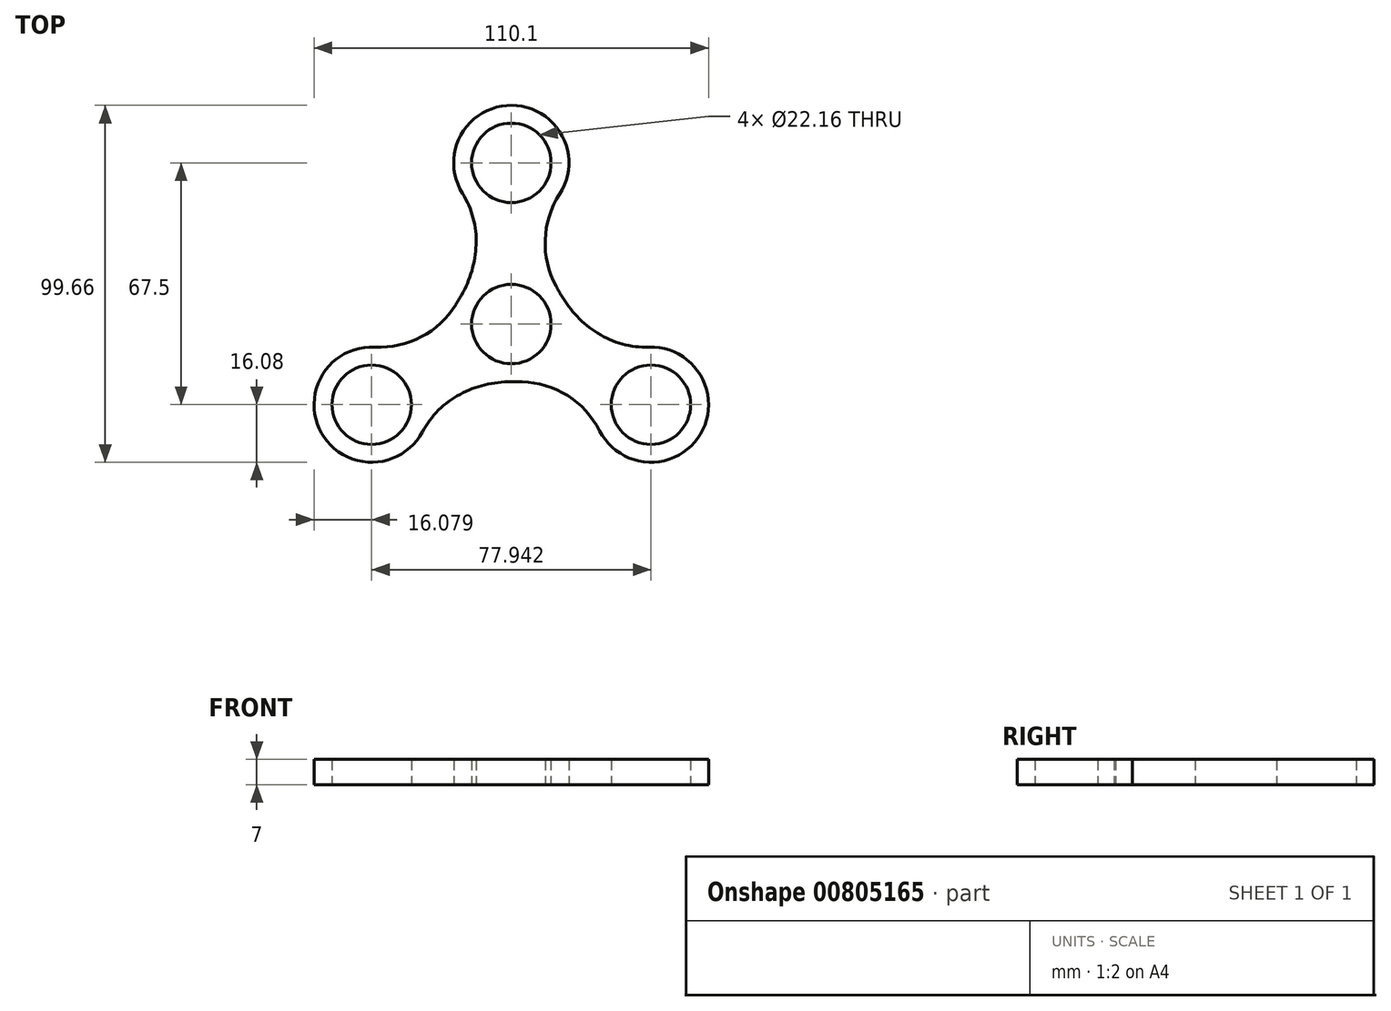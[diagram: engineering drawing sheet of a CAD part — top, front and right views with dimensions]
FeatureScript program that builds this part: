
annotation { "Feature Type Name" : "Feature", "Feature Type Description" : "" }
export const myFeature = defineFeature(function(context is Context, id is Id, definition is map)
    precondition{}
    {
        {
            var Q0;
            Q0=qCreatedBy(makeId("Top.planeOp"),FACE);
            var sketch = newSketch(context, id + "F0", { "sketchPlane" : qUnion([Q0])});
            skCircle(sketch, "E0", {"center": v(0, 0) * mm, "radius": 16.08 * mm});
            skLineSegment(sketch, "E1", {"start": v(0, 0) * mm, "end": v(0, 45) * mm, "construction": true});
            skLineSegment(sketch, "E2.1.0", {"start": v(0, 0) * mm, "end": v(-38.97, -22.5) * mm, "construction": true});
            skLineSegment(sketch, "E2.2.0", {"start": v(0, 0) * mm, "end": v(38.97, -22.5) * mm, "construction": true});
            skArc(sketch, "E3", {"start": v(-38.97, -22.5) * mm, "mid": v(-13.93, 8.04) * mm, "end": v(0, 45) * mm});
            skCircle(sketch, "E4", {"center": v(0, 0) * mm, "radius": 11.08 * mm});
            skArc(sketch, "E5", {"start": v(0, 45) * mm, "mid": v(13.93, 8.04) * mm, "end": v(38.97, -22.5) * mm});
            skArc(sketch, "E6", {"start": v(38.97, -22.5) * mm, "mid": v(0, -16.08) * mm, "end": v(-38.97, -22.5) * mm});
            skCircle(sketch, "E7", {"center": v(0, 45) * mm, "radius": 11.08 * mm});
            skCircle(sketch, "E8", {"center": v(0, 45) * mm, "radius": 16.08 * mm});
            skCircle(sketch, "E9.1.0", {"center": v(-38.97, -22.5) * mm, "radius": 16.08 * mm});
            skCircle(sketch, "E9.1.1", {"center": v(-38.97, -22.5) * mm, "radius": 11.08 * mm});
            skCircle(sketch, "E9.2.0", {"center": v(38.97, -22.5) * mm, "radius": 16.08 * mm});
            skCircle(sketch, "E9.2.1", {"center": v(38.97, -22.5) * mm, "radius": 11.08 * mm});
            skLineSegment(sketch, "E10", {"start": v(-30.41, 33.92) * mm, "end": v(35.6, 33.92) * mm, "construction": true});
            skArc(sketch, "E11", {"start": v(-13.93, 8.04) * mm, "mid": v(-9.92, 20.73) * mm, "end": v(-11.65, 33.92) * mm});
            skLineSegment(sketch, "E12", {"start": v(-119.14, 68.79) * mm, "end": v(0, -137.57) * mm, "construction": true});
            skLineSegment(sketch, "E13", {"start": v(0, -137.57) * mm, "end": v(119.14, 68.79) * mm, "construction": true});
            skLineSegment(sketch, "E14", {"start": v(119.14, 68.79) * mm, "end": v(-119.14, 68.79) * mm, "construction": true});
            skArc(sketch, "E15.MirrorCS", {"start": v(13.93, 8.04) * mm, "mid": v(9.92, 20.73) * mm, "end": v(11.65, 33.92) * mm});
            skArc(sketch, "E16.1.0", {"start": v(0, -16.08) * mm, "mid": v(-12.99, -18.96) * mm, "end": v(-23.55, -27.05) * mm});
            skArc(sketch, "E16.1.1", {"start": v(-13.93, 8.04) * mm, "mid": v(-22.91, -1.77) * mm, "end": v(-35.2, -6.87) * mm});
            skArc(sketch, "E16.2.0", {"start": v(13.93, 8.04) * mm, "mid": v(22.91, -1.77) * mm, "end": v(35.2, -6.87) * mm});
            skArc(sketch, "E16.2.1", {"start": v(0, -16.08) * mm, "mid": v(12.99, -18.96) * mm, "end": v(23.55, -27.05) * mm});
            skSolve(sketch);
        }
        {
            var Q0;
            {var subQ0=sQuery(id+"F0.wireOp",EDGE,"E8");var subQ2=sQuery(id+"F0.wireOp",EDGE,"E3");var subQ3=makeQuery(id+"F0.imprint","INTERSECT",VERTEX,{"derivedFrom":[subQ2,subQ0]});Q0=makeQuery(id+"F0.imprint","IMPRINT",FACE,{"disambiguationData":[TD([[makeQuery(id+"F0.imprint","IMPRINT",EDGE,{"disambiguationData":[TD([[subQ3,-1.0]])],"derivedFrom":subQ2}),1.0]])]});}
            var Q1;
            {var subQ0=sQuery(id+"F0.wireOp",EDGE,"E11");Q1=makeQuery(id+"F0.imprint","IMPRINT",FACE,{"disambiguationData":[TD([[makeQuery(id+"F0.imprint","IMPRINT",EDGE,{"derivedFrom":subQ0}),-1.0]])]});}
            var Q2;
            {var subQ0=sQuery(id+"F0.wireOp",EDGE,"E8");var subQ1=sQuery(id+"F0.wireOp",EDGE,"E3");var subQ2=makeQuery(id+"F0.imprint","INTERSECT",VERTEX,{"derivedFrom":[subQ1,subQ0]});Q2=makeQuery(id+"F0.imprint","IMPRINT",FACE,{"disambiguationData":[TD([[makeQuery(id+"F0.imprint","IMPRINT",EDGE,{"disambiguationData":[TD([[subQ2,-1.0]])],"derivedFrom":subQ1}),-1.0]])]});}
            var Q3;
            {var subQ0=sQuery(id+"F0.wireOp",EDGE,"E3");var subQ5=sQuery(id+"F0.wireOp",EDGE,"E8");var subQ6=makeQuery(id+"F0.imprint","INTERSECT",VERTEX,{"derivedFrom":[subQ0,subQ5]});Q3=makeQuery(id+"F0.imprint","IMPRINT",FACE,{"disambiguationData":[TD([[makeQuery(id+"F0.imprint","IMPRINT",EDGE,{"disambiguationData":[TD([[subQ6,-1.0]])],"derivedFrom":subQ5}),-1.0]])]});}
            var Q4;
            {var subQ0=sQuery(id+"F0.wireOp",EDGE,"E15.MirrorCS");Q4=makeQuery(id+"F0.imprint","IMPRINT",FACE,{"disambiguationData":[TD([[makeQuery(id+"F0.imprint","IMPRINT",EDGE,{"derivedFrom":subQ0}),1.0]])]});}
            var Q5;
            {var subQ5=sQuery(id+"F0.wireOp",EDGE,"E3");var subQ7=sQuery(id+"F0.wireOp",EDGE,"E9.1.1");var subQ9=makeQuery(id+"F0.imprint","INTERSECT",VERTEX,{"derivedFrom":[subQ5,subQ7]});Q5=makeQuery(id+"F0.imprint","IMPRINT",FACE,{"disambiguationData":[TD([[makeQuery(id+"F0.imprint","IMPRINT",EDGE,{"disambiguationData":[TD([[subQ9,-1.0]])],"derivedFrom":subQ5}),1.0]])]});}
            var Q6;
            {var subQ0=sQuery(id+"F0.wireOp",EDGE,"E9.1.1");var subQ1=sQuery(id+"F0.wireOp",EDGE,"E3");var subQ2=makeQuery(id+"F0.imprint","INTERSECT",VERTEX,{"derivedFrom":[subQ1,subQ0]});Q6=makeQuery(id+"F0.imprint","IMPRINT",FACE,{"disambiguationData":[TD([[makeQuery(id+"F0.imprint","IMPRINT",EDGE,{"disambiguationData":[TD([[subQ2,-1.0]])],"derivedFrom":subQ1}),-1.0]])]});}
            var Q7;
            {var subQ0=sQuery(id+"F0.wireOp",EDGE,"E16.1.1");Q7=makeQuery(id+"F0.imprint","IMPRINT",FACE,{"disambiguationData":[TD([[makeQuery(id+"F0.imprint","IMPRINT",EDGE,{"derivedFrom":subQ0}),1.0]])]});}
            var Q8;
            {var subQ0=sQuery(id+"F0.wireOp",EDGE,"E3");var subQ5=sQuery(id+"F0.wireOp",EDGE,"E9.1.0");var subQ6=makeQuery(id+"F0.imprint","INTERSECT",VERTEX,{"derivedFrom":[subQ0,subQ5]});Q8=makeQuery(id+"F0.imprint","IMPRINT",FACE,{"disambiguationData":[TD([[makeQuery(id+"F0.imprint","IMPRINT",EDGE,{"disambiguationData":[TD([[subQ6,1.0]])],"derivedFrom":subQ5}),-1.0]])]});}
            var Q9;
            {var subQ0=sQuery(id+"F0.wireOp",EDGE,"E16.1.0");Q9=makeQuery(id+"F0.imprint","IMPRINT",FACE,{"disambiguationData":[TD([[makeQuery(id+"F0.imprint","IMPRINT",EDGE,{"derivedFrom":subQ0}),-1.0]])]});}
            var Q10;
            {var subQ0=sQuery(id+"F0.wireOp",EDGE,"E5");var subQ5=sQuery(id+"F0.wireOp",EDGE,"E9.2.0");var subQ6=makeQuery(id+"F0.imprint","INTERSECT",VERTEX,{"derivedFrom":[subQ0,subQ5]});Q10=makeQuery(id+"F0.imprint","IMPRINT",FACE,{"disambiguationData":[TD([[makeQuery(id+"F0.imprint","IMPRINT",EDGE,{"disambiguationData":[TD([[subQ6,-1.0]])],"derivedFrom":subQ5}),-1.0]])]});}
            var Q11;
            {var subQ0=sQuery(id+"F0.wireOp",EDGE,"E16.2.1");Q11=makeQuery(id+"F0.imprint","IMPRINT",FACE,{"disambiguationData":[TD([[makeQuery(id+"F0.imprint","IMPRINT",EDGE,{"derivedFrom":subQ0}),1.0]])]});}
            var Q12;
            {var subQ0=sQuery(id+"F0.wireOp",EDGE,"E16.2.0");Q12=makeQuery(id+"F0.imprint","IMPRINT",FACE,{"disambiguationData":[TD([[makeQuery(id+"F0.imprint","IMPRINT",EDGE,{"derivedFrom":subQ0}),-1.0]])]});}
            var Q13;
            {var subQ0=sQuery(id+"F0.wireOp",EDGE,"E9.2.0");var subQ4=sQuery(id+"F0.wireOp",EDGE,"E5");var subQ5=makeQuery(id+"F0.imprint","INTERSECT",VERTEX,{"derivedFrom":[subQ4,subQ0]});Q13=makeQuery(id+"F0.imprint","IMPRINT",FACE,{"disambiguationData":[TD([[makeQuery(id+"F0.imprint","IMPRINT",EDGE,{"disambiguationData":[TD([[subQ5,-1.0]])],"derivedFrom":subQ4}),1.0]])]});}
            var Q14;
            {var subQ0=sQuery(id+"F0.wireOp",EDGE,"E9.2.0");var subQ1=sQuery(id+"F0.wireOp",EDGE,"E5");var subQ2=makeQuery(id+"F0.imprint","INTERSECT",VERTEX,{"derivedFrom":[subQ1,subQ0]});Q14=makeQuery(id+"F0.imprint","IMPRINT",FACE,{"disambiguationData":[TD([[makeQuery(id+"F0.imprint","IMPRINT",EDGE,{"disambiguationData":[TD([[subQ2,-1.0]])],"derivedFrom":subQ1}),-1.0]])]});}
            var Q15;
            Q15=makeQuery(id+"F0.imprint","IMPRINT",FACE,{"disambiguationData":[TD([[makeQuery(id+"F0.imprint","IMPRINT",EDGE,{"derivedFrom":sQuery(id+"F0.wireOp",EDGE,"E4")}),-1.0]])]});
            extrude(context, id + "F1", {"entities" : qUnion([Q0, Q1, Q2, Q3, Q4, Q5, Q6, Q7, Q8, Q9, Q10, Q11, Q12, Q13, Q14, Q15]), "depth" : 7 * mm, "offsetDistance" : 25 * mm});
        }
        {
            var Q0;
            Q0=makeQuery(id+"F1.opExtrude","SWEPT_EDGE",EDGE,{"disambiguationData":[OSD([sQuery(id+"F0.wireOp",EDGE,"E8"),sQuery(id+"F0.wireOp",EDGE,"E15.MirrorCS")])]});
            var Q1;
            Q1=makeQuery(id+"F1.opExtrude","SWEPT_EDGE",EDGE,{"disambiguationData":[OSD([sQuery(id+"F0.wireOp",EDGE,"E8"),sQuery(id+"F0.wireOp",EDGE,"E11")])]});
            var Q2;
            Q2=makeQuery(id+"F1.opExtrude","SWEPT_EDGE",EDGE,{"disambiguationData":[OSD([sQuery(id+"F0.wireOp",EDGE,"E9.2.0"),sQuery(id+"F0.wireOp",EDGE,"E16.2.0")])]});
            var Q3;
            Q3=makeQuery(id+"F1.opExtrude","SWEPT_EDGE",EDGE,{"disambiguationData":[OSD([sQuery(id+"F0.wireOp",EDGE,"E9.2.0"),sQuery(id+"F0.wireOp",EDGE,"E16.2.1")])]});
            var Q4;
            Q4=makeQuery(id+"F1.opExtrude","SWEPT_EDGE",EDGE,{"disambiguationData":[OSD([sQuery(id+"F0.wireOp",EDGE,"E9.1.0"),sQuery(id+"F0.wireOp",EDGE,"E16.1.0")])]});
            var Q5;
            Q5=makeQuery(id+"F1.opExtrude","SWEPT_EDGE",EDGE,{"disambiguationData":[OSD([sQuery(id+"F0.wireOp",EDGE,"E9.1.0"),sQuery(id+"F0.wireOp",EDGE,"E16.1.1")])]});
            fillet(context, id + "F2", {"entities" : qUnion([Q0, Q1, Q2, Q3, Q4, Q5]), "radius" : 25 * mm, "tangentPropagation" : true, "allowEdgeOverflow" : false});
        }
    });
